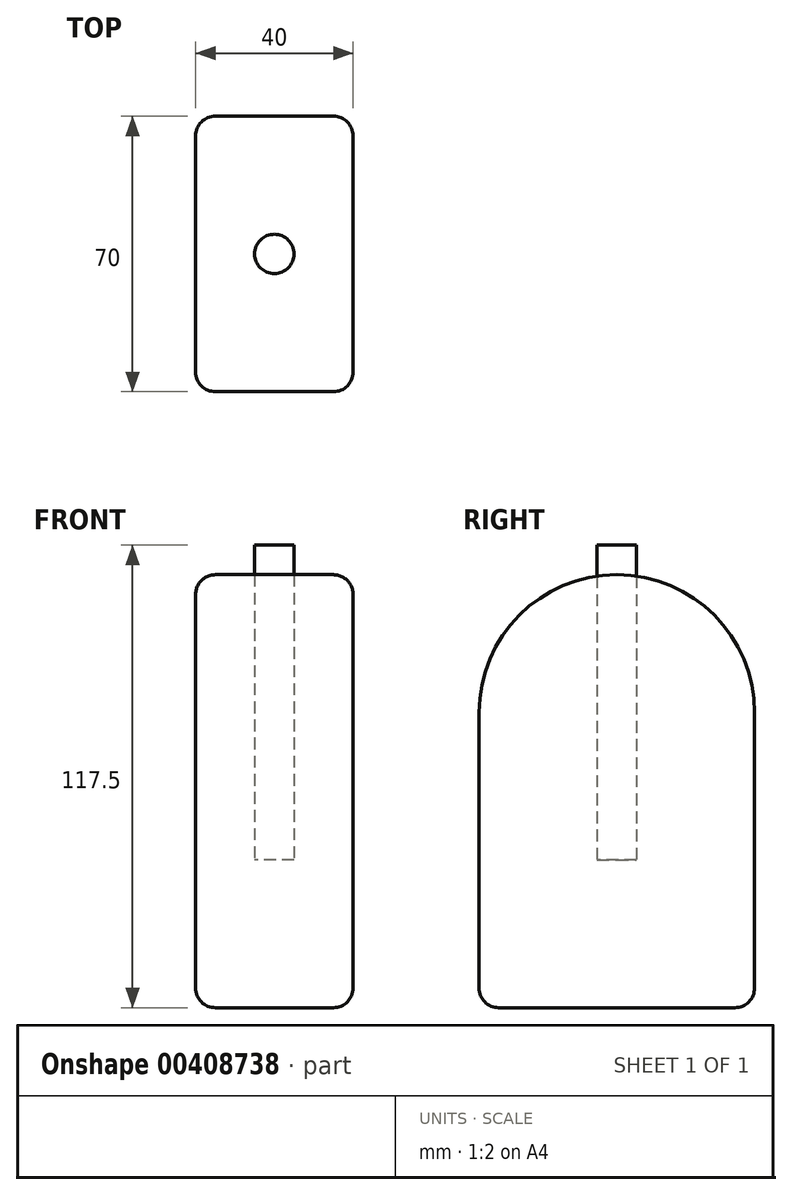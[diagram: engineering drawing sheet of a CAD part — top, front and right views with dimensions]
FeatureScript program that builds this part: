
annotation { "Feature Type Name" : "Feature", "Feature Type Description" : "" }
export const myFeature = defineFeature(function(context is Context, id is Id, definition is map)
    precondition{}
    {
        {
            var Q0;
            Q0=qCreatedBy(makeId("Right.planeOp"),FACE);
            var sketch = newSketch(context, id + "F0", { "sketchPlane" : qUnion([Q0])});
            skLineSegment(sketch, "E0.bottom", {"start": v(35, -37.5) * mm, "end": v(-35, -37.5) * mm});
            skLineSegment(sketch, "E0.top", {"start": v(35, 37.5) * mm, "end": v(-35, 37.5) * mm});
            skLineSegment(sketch, "E0.left", {"start": v(35, -37.5) * mm, "end": v(35, 37.5) * mm});
            skLineSegment(sketch, "E0.right", {"start": v(-35, -37.5) * mm, "end": v(-35, 37.5) * mm});
            skPoint(sketch, "E0.middle", {"position": v(0, 0) * mm});
            skCircle(sketch, "E1", {"center": v(0, 37.5) * mm, "radius": 35 * mm});
            skSolve(sketch);
        }
        {
            var Q0;
            Q0=makeQuery(id+"F0.imprint","IMPRINT",FACE,{"disambiguationData":[TD([[makeQuery(id+"F0.imprint","IMPRINT",EDGE,{"derivedFrom":sQuery(id+"F0.wireOp",EDGE,"E0.bottom")}),-1.0]])]});
            var Q1;
            {var subQ0=sQuery(id+"F0.wireOp",EDGE,"E0.top");Q1=makeQuery(id+"F0.imprint","IMPRINT",FACE,{"disambiguationData":[TD([[makeQuery(id+"F0.imprint","IMPRINT",EDGE,{"derivedFrom":subQ0}),1.0]])]});}
            var Q2;
            {var subQ0=sQuery(id+"F0.wireOp",EDGE,"E0.top");Q2=makeQuery(id+"F0.imprint","IMPRINT",FACE,{"disambiguationData":[TD([[makeQuery(id+"F0.imprint","IMPRINT",EDGE,{"derivedFrom":subQ0}),-1.0]])]});}
            extrude(context, id + "F1", {"entities" : qUnion([Q0, Q1, Q2]), "depth" : 40 * mm});
        }
        {
            var Q0;
            Q0=makeQuery(id+"F1.opExtrude","CAP_EDGE",EDGE,{"disambiguationData":[OSD([sQuery(id+"F0.wireOp",EDGE,"E0.right")])],"isStart":false});
            fillet(context, id + "F2", {"entities" : qUnion([Q0]), "radius" : 5 * mm, "tangentPropagation" : true, "allowEdgeOverflow" : false});
        }
        {
            var Q0;
            Q0=makeQuery(id+"F1.opExtrude","SWEPT_EDGE",EDGE,{"disambiguationData":[OSD([sQuery(id+"F0.wireOp",EDGE,"E0.bottom"),sQuery(id+"F0.wireOp",EDGE,"E0.right")])]});
            fillet(context, id + "F3", {"entities" : qUnion([Q0]), "radius" : 5 * mm, "tangentPropagation" : true, "allowEdgeOverflow" : false});
        }
        {
            var Q0;
            Q0=makeQuery(id+"F1.opExtrude","CAP_EDGE",EDGE,{"disambiguationData":[OSD([sQuery(id+"F0.wireOp",EDGE,"E0.bottom")])],"isStart":true});
            fillet(context, id + "F4", {"entities" : qUnion([Q0]), "radius" : 5 * mm, "tangentPropagation" : true, "allowEdgeOverflow" : false});
        }
        {
            var Q0;
            Q0=qCreatedBy(makeId("Top.planeOp"),FACE);
            var sketch = newSketch(context, id + "F5", { "sketchPlane" : qUnion([Q0])});
            skCircle(sketch, "E2", {"center": v(20, 0) * mm, "radius": 5 * mm});
            skSolve(sketch);
        }
        {
            var Q0;
            Q0=makeQuery(id+"F5.imprint","IMPRINT",FACE,{"disambiguationData":[TD([[makeQuery(id+"F5.imprint","IMPRINT",EDGE,{"derivedFrom":sQuery(id+"F5.wireOp",EDGE,"E2")}),1.0]])]});
            extrude(context, id + "F6", {"entities" : qUnion([Q0]), "depth" : 80 * mm});
        }
    });
